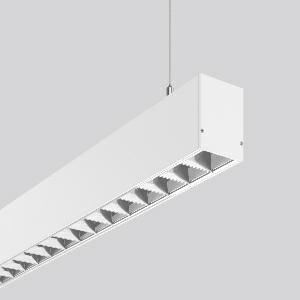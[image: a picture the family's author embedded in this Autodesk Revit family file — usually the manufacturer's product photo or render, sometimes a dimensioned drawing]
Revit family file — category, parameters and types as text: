
# Revit family: less_is_more_50_312335_002_1_a5a2
name_source: partatom
category: Lighting Fixtures
units: mm (PartAtom-declared; Revit-internal decimal feet)

## family parameters
Cut with Voids When Loaded = No
Host = Face
Light Source = No
Part Type = Normal
Room Calculation Point = No
Round Connector Dimension = Use Diameter
Shared = No

## types (1)
- LESS IS MORE 50 (1 x LED Modul 840, 2650 lm, 4000)
    Apparent Load = 22 VA
    CIE Flux Codes = 95 100 100 100 100
    Color Rendering = 80
    Color Temperature = 4000
    Default Elevation = 1800 mm
    Description = Series: LESS IS MORE 50
Linear pendant luminaire for aesthetically sophisticated lighting. Housing: extruded aluminium profile, powder-coated. End cap aluminium powder-coated. Canopy made of aluminium, powder-coated. Alea optical system: Reflector structure (ABS, Aluminium-coated, highly polished) with integrated diffuser made of non-yellowing plastic (PMMA) opal for glare-free light at the workstation (screen-compliant according to EN 12464-1). Direct light emission. Suitable for pendant. 2-point steel cable suspension freely positionable and infinitely height-adjustable. Special lengths available on request. LED unit with integrated converter interchangeable and removable. Suitable for through-wiring. With sensors or as a safety luminaire on request. 
Colour: traffic white, matt (RAL 9016)
Length: 847 mm
Width: 57 mm
Height: 75 mm
Suspension length: 2000 mm
Lamp: LED
Socket: without socket
Colour temperature: 4000K
Colour rendering index (CRI): 80
System power: 22 W
Rated luminous flux: 2650 lm
Luminous efficiency: 120 lm/W
Control gear: Regulated power supply
Protection class: I
Type of protection: IP 20
    Height = 75 mm
    Lamp = 1 x LED Modul 840
    Lamp Light Flux = 2650 lm
    Lamp count = 1
    Length = 847 mm
    Lifetime = 50000 h
    Luminous efficacy = 120 lm/W
    Manufacturer = RZB
    ModVariant = No
    Model = 312335.002.1
    Mounting Place = Ceiling
    Mounting Type = Pendant
    Number of Poles = 1
    OnlyDefault = Yes
    Power Factor = 1
    Product Name = LESS IS MORE 50
    Product group = Pendant LED linear luminaires
    ProductGroupID = 907
    Protection Class = Protection class I
    Protection Degree = IP 20
    RLX_Detail_Level = 1
    RLX_Emergency_Light_Flux = 0 lm
    RLX_Emergency_Type = 0
    RLX_Emergency_Type_DB = No
    RlxData = <blob elided: 33137 chars, md5=88600794>
    Socket = socket
    Standby Power = 0 W
    System Light Flux = 2650 lm
    System Power = 22 W
    Type Comments = Product without accessories
    Type Image = 312342.002.jpg
    URL = http://relux.com
    VarID = ---
    Voltage = 230 V
    Voltage Range = 220-240 V
    Weight = 0.00 kg
    Width = 57 mm

## geometry (parser evidence)
native form markers: Blend x4, Sweep x10
no freeform markers — native parametric forms only
